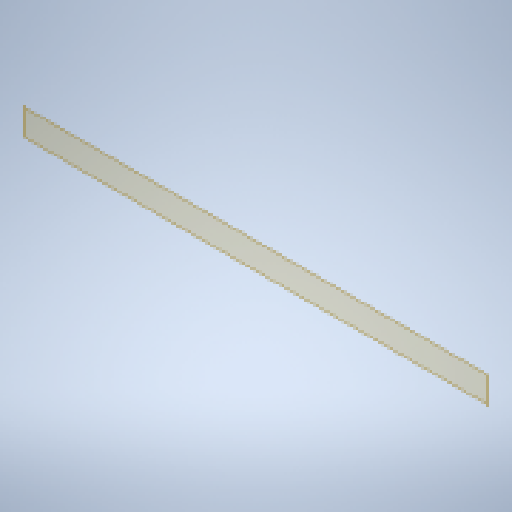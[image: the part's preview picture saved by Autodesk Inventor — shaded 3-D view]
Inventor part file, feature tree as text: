
AUTODESK INVENTOR PART (.ipt)
format: ipt  version: 2025 (Build 290162000, 162)  size: 121,856 bytes
history: native  units: in
note: dims shown in document units (in); Inventor stores cm internally (conversion verified against a paired STEP export)
features: other x3, plane x1
ambient origin geometry x8: Origin, YZ Plane, XZ Plane, XY Plane, X Axis, Y Axis, Z Axis, Center Point
feature tree (4):
  plane  "Work Plane1"
  other  "<userpath>\OneDrive\Documents\TigerBurn\USCTigerBurn24\v1\Tiger.iam"
  other  "Tiger.iam"
  other  "4x4x72:32"
